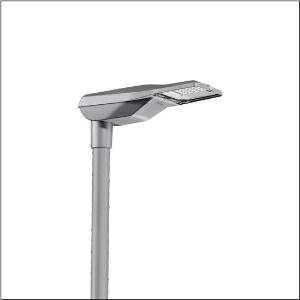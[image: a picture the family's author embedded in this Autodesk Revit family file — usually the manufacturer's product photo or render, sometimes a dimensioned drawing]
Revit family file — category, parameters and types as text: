
# Revit family: streetlight_sl_21_micro___st1_5a_5xe5p43a08db_8088
name_source: partatom
category: Lighting Fixtures
units: mm (PartAtom-declared; Revit-internal decimal feet)

## family parameters
Cut with Voids When Loaded = No
Host = Face
Light Source = No
Part Type = Normal
Room Calculation Point = No
Round Connector Dimension = Use Diameter
Shared = No

## types (1)
- --- (1 x LED, 5230 lm, 39.1 W, 4000K)
    Apparent Load = 39 VA
    CIE Flux Codes = 22 53 95 100 100
    Color Rendering = 70
    Color Temperature = 4000K
    Default Elevation = 1800 mm
    Description = Streetlight SL 21 micro, mast luminaire, primary light control with lens, of PMMA, primary optical cover: cover, of toughened safety glass, transparent, light distribution: ST1.5a, light emission: direct distribution, primary light characteristic: asymmetric, installation type: side-entry, post-top, LED, 3G 1.5mm², High Power LED, rated luminous flux: 5.230lm, luminous efficacy: 134lm/W, light colour: 740, colour temperature: 4000K, control: flexible luminous flux parameterisation, time-dependent luminous flux control, constant luminous flux control, overheat protection, mains connection: 230..240V, AC, 50/60Hz, connection cable pre-assembled, cable length: 6,5m, wiring characteristics: H07RN-F, start of lifetime: 39W, end of service life: 41W, reduction: 18W, luminaire housing, of diecast aluminium, powder-coated, Siteco® metallic grey (DB 702S), corrosivity category C5 mid according to DIN EN ISO 12944, please order mast flange separately, inclination adjustable: 0°, 5°, 10°, 15°, sealing non-destructively replaceable, multi-level sealing system, length: 528mm, width: 235mm, height: 110mm, mast flange for spigot size: 42mm (side-entry): 5XC10008XM4, 60/48mm (side-entry/post-top): 5XC10108XM2, 76/60mm (side-entry/post-top): 5XC10108XM1, protection rating (complete): IP66, insulation class (complete): insulation class II (safety insulation), certification: CE, ENEC, ENEC+, VDE, impact resistance: IK09, permissible operating ambient temperature for outdoor applications: -40..+50°C, standard-compliant lighting for roads and squares, packaging unit: 1 piece

Light Distribution: ST1.5a
    Height = 110 mm
    Lamp = 1 x LED
    Lamp Light Flux = 5230 lm
    Lamp Power = 39.1 W
    Lamp count = 1
    Length = 528 mm
    Luminous efficacy = 134 lm/W
    Manufacturer = Siteco
    ModVariant = No
    Model = 5XE5P43A08DB
    Number of Poles = 1
    OnlyDefault = Yes
    Power Factor = 1
    Product Name = Streetlight SL 21 micro | ST1.5a
    Product group = mast luminaire | pylon top
    ProductGroupID = 6100
    Protection Class = Protection class II
    Protection Degree = IP 66
    RLX_Detail_Level = 1
    RLX_Emergency_Light_Flux = 0 lm
    RLX_Emergency_Type = 0
    RLX_Emergency_Type_DB = No
    RlxData = <blob elided: 102669 chars, md5=cfb5c705>
    Socket = socket
    Standby Power = 0 W
    System Light Flux = 5230 lm
    System Power = 39 W
    Type Comments = factory setting: luminous flux: 100 % | Output Level: 100 % | 765 mA
    Type Image = l_1006881.jpg
    URL = http://relux.com
    VarID = @adj_103663
    Voltage = 0 V
    Weight = 0.00 kg
    Width = 235 mm

## geometry (parser evidence)
native form markers: Blend x4, Sweep x9
no freeform markers — native parametric forms only
